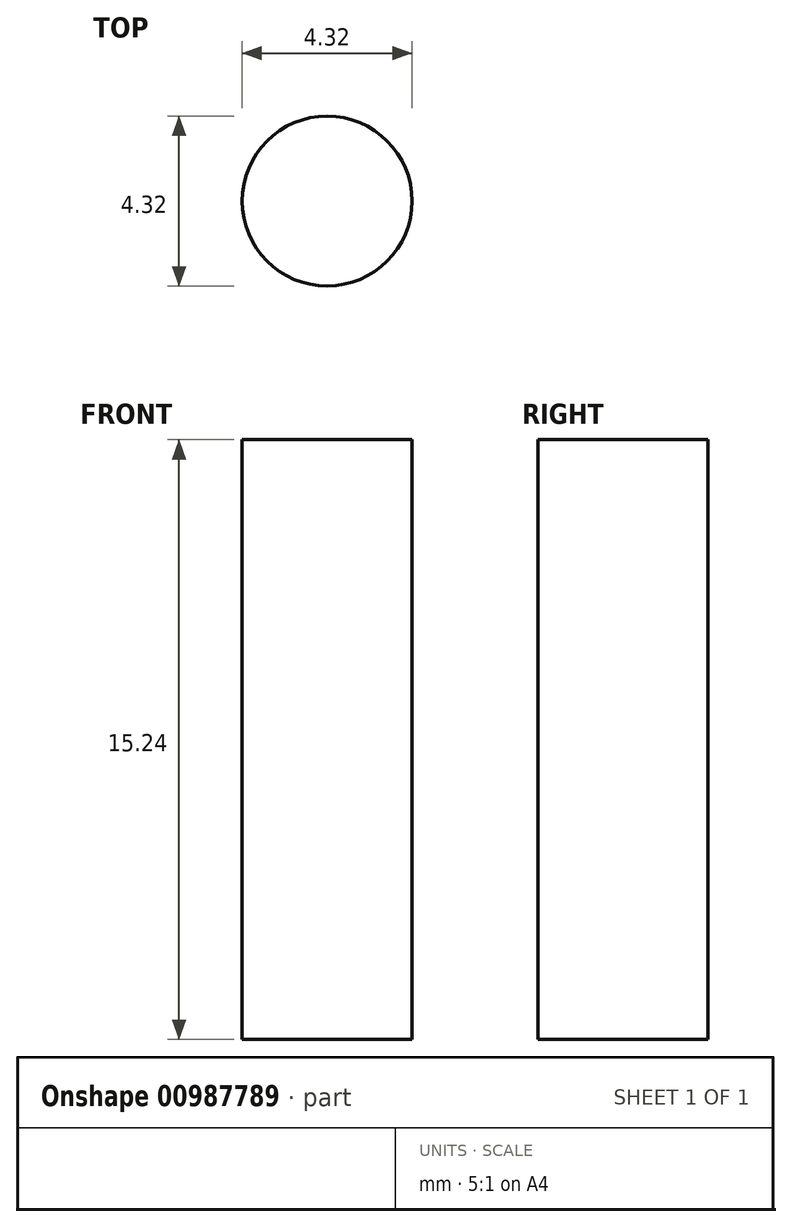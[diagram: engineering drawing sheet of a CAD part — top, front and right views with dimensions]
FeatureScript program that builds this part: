
annotation { "Feature Type Name" : "Feature", "Feature Type Description" : "" }
export const myFeature = defineFeature(function(context is Context, id is Id, definition is map)
    precondition{}
    {
        {
            var Q0;
            Q0=qCreatedBy(makeId("Top.planeOp"),FACE);
            var sketch = newSketch(context, id + "F0", { "sketchPlane" : qUnion([Q0])});
            skCircle(sketch, "E0", {"center": v(0, 0) * mm, "radius": 2.16 * mm});
            skSolve(sketch);
        }
        {
            var Q0;
            Q0 = qSketchRegion(id + "F0", true);
            extrude(context, id + "F1", {"entities" : qUnion([Q0]), "depth" : 15.24 * mm, "offsetDistance" : 25.4 * mm});
        }
    });
